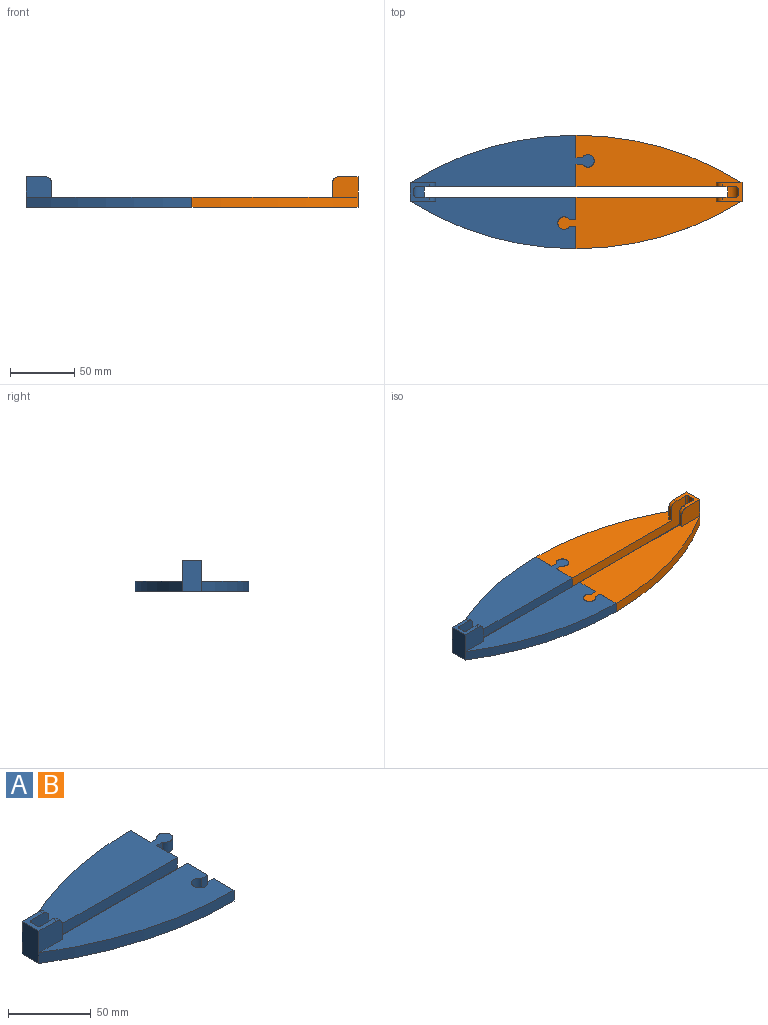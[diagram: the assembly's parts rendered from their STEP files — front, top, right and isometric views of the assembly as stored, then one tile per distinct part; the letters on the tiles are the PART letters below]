
ASSEMBLY  parts=2 mates=1
PART A: 32 faces, bbox 144.5x89.3x25.8 mm
  f0: plane 144.45x89.34mm, normal (0,0,-1), area 7374.8mm2, adj f1,f2,f3,f4,f7,f8,f15,f16
  f1: plane 17.64x8mm, normal (1,0,0), area 141.1mm2, adj f0,f4,f5,f27
  f2: plane 17.54x8mm, normal (1,0,0), area 140.3mm2, adj f0,f6,f7,f24
  f3: plane 124.6x24mm, normal (0,1,0), area 1221.9mm2, adj f0,f6,f11,f13,f16,f17,f19,f21
  f4: plane 124.6x24mm, normal (0,-1,0), area 1221.9mm2, adj f0,f1,f5,f11,f14,f16,f17,f18
  f5: plane 143.77x40.09mm, normal (0,0,1), area 3683.9mm2, adj f1,f4,f8,f9,f18,f22,f27,f28
  f6: plane 129.6x40.08mm, normal (0,0,1), area 3483.5mm2, adj f2,f3,f7,f10,f19,f23,f24,f25
  f7: cylinder r=245mm len=129.6mm, axis (0,0,-1), area 1092.5mm2, adj f0,f2,f6,f15
  f8: cylinder r=245mm len=129.6mm, axis (0,0,-1), area 1092.5mm2, adj f0,f5,f15,f22
  f9: plane 20x16mm, normal (0,1,0), area 314.6mm2, adj f5,f11,f15,f18,f20
  f10: plane 20x16mm, normal (0,-1,0), area 314.6mm2, adj f6,f11,f15,f19,f21
  f11: plane 15x14.4mm, normal (0,0,1), area 116.9mm2, adj f3,f4,f9,f10,f12,f13,f14,f15
  f12: plane 15.25x4.4mm, normal (1,0,0), area 67.1mm2, adj f11,f13,f14,f17
  f13: cylinder r=2mm len=20.54mm, axis (0,0,1), area 56.2mm2, adj f3,f11,f12,f17
  f14: cylinder r=2mm len=20.54mm, axis (0,0,-1), area 56.2mm2, adj f4,f11,f12,f17
  f15: plane 24x14.4mm, normal (-1,0,0), area 345.6mm2, adj f0,f7,f8,f9,f10,f11
  f16: plane 8.4x0.75mm, normal (1,0,0), area 6.3mm2, adj f0,f3,f4,f17
  f17: cylinder r=8mm len=8.4mm, axis (0,1,0), area 94mm2, adj f3,f4,f12,f13,f14,f16
  f18: plane 11x3mm, normal (1,0,0), area 33mm2, adj f4,f5,f9,f20
  f19: plane 11x3mm, normal (1,0,0), area 33mm2, adj f3,f6,f10,f21
  f20: cylinder r=5mm len=5mm, axis (0,1,0), area 23.6mm2, adj f4,f9,f11,f18
  f21: cylinder r=5mm len=5mm, axis (0,1,0), area 23.6mm2, adj f3,f10,f11,f19
  f22: plane 17.64x8mm, normal (1,0,0), area 141.1mm2, adj f0,f5,f8,f28
  f23: plane 17.54x8mm, normal (1,0,0), area 140.3mm2, adj f0,f3,f6,f25
  f24: plane 8x5mm, normal (0,1,0), area 40mm2, adj f0,f2,f6,f26
  f25: plane 8x5mm, normal (0,-1,0), area 40mm2, adj f0,f6,f23,f26
  f26: cylinder r=5mm len=10mm, axis (0,0,1), area 209.4mm2, adj f0,f6,f24,f25
  f27: plane 8x5.2mm, normal (0,-1,0), area 41.2mm2, adj f0,f1,f5,f29
  f28: plane 8x5.05mm, normal (0,1,0), area 40.4mm2, adj f0,f5,f22,f30,f31
  f29: bspline ~15.58x9.06mm, area 201.6mm2, adj f0,f5,f27,f31
  f30: plane 7.4x0.07mm, normal (0.49,0.87,0), area 0.3mm2, adj f0,f28,f31
  f31: bspline ~9.43x0.16mm, area 0.6mm2, adj f0,f5,f28,f29,f30
PART B: same geometry as A
PLACE A at identity fixed
PLACE B rot(axis=(0,0,1),180deg) t=(0,0,0)mm
MATE fastened B.f6 <-> A.f5  axis (0,0,1) through (0,44.28,8)mm
